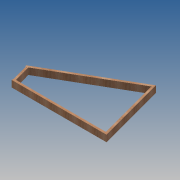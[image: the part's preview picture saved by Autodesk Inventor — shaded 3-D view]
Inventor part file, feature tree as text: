
AUTODESK INVENTOR PART (.ipt)
format: ipt  version: 2014 SP1 (Build 180222100, 222)  size: 126,976 bytes
history: native  units: in
note: dims shown in document units (in); Inventor stores cm internally (conversion verified against a paired STEP export)
features: extrude x5, sketch x5
ambient origin geometry x8: Origin, YZ Plane, XZ Plane, XY Plane, X Axis, Y Axis, Z Axis, Center Point
bodies: Body1 (feature_tree)
feature tree (10):
  extrude  "Extrusion2"  TaperAngle=150.0deg  [1 undecoded]
  extrude  "Extrusion3"  Depth=1.9685in
  extrude  "Extrusion4"  Depth=48.0315in
  extrude  "Extrusion5"  TaperAngle=30.0deg  [1 undecoded]
  extrude  "Extrusion6"  Depth=4.4882in TaperAngle=0.0deg
  sketch  "Sketch1"  dims[d1=118.1102in d2=150.0deg]
  sketch  "Sketch2"  dims[d3=39.3701in d11=1.9685in]
  sketch  "Sketch3"  dims[d12=65.3543in d13=48.0315in]
  sketch  "Sketch4"  dims[d14=75.0deg d16=30.0deg]
  sketch  "Sketch5"  dims[d19=1.4961in d20=1.4961in d21=4.4882in d22=0.0in d23=4.4882in d24=0.0in d25=137.7953in d26=0.0in d27=0.0394in d28=0.0in d29=0.0394in d30=0.0in]
note: 2 required parameter values undecoded (feature->parameter linkage not recoverable at this tier; creation-order binding heuristic only, values carry confidence <= 0.55)
